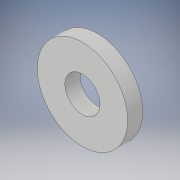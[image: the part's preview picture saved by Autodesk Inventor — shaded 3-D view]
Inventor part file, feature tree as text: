
AUTODESK INVENTOR PART (.ipt)
format: ipt  version: 2019 (Build 230136000, 136)  size: 191,488 bytes
history: native  units: mm
features: extrude x1, sketch x1
ambient origin geometry x8: Origin, YZ Plane, XZ Plane, XY Plane, X Axis, Y Axis, Z Axis, Center Point
bodies: Solid1 (feature_tree)
feature tree (2):
  extrude  "Extrusion1"  Depth=1.5mm
  sketch  "Sketch1"  dims[d0=3.5mm d1=9.0mm d2=1.5mm d3=0.0mm]
